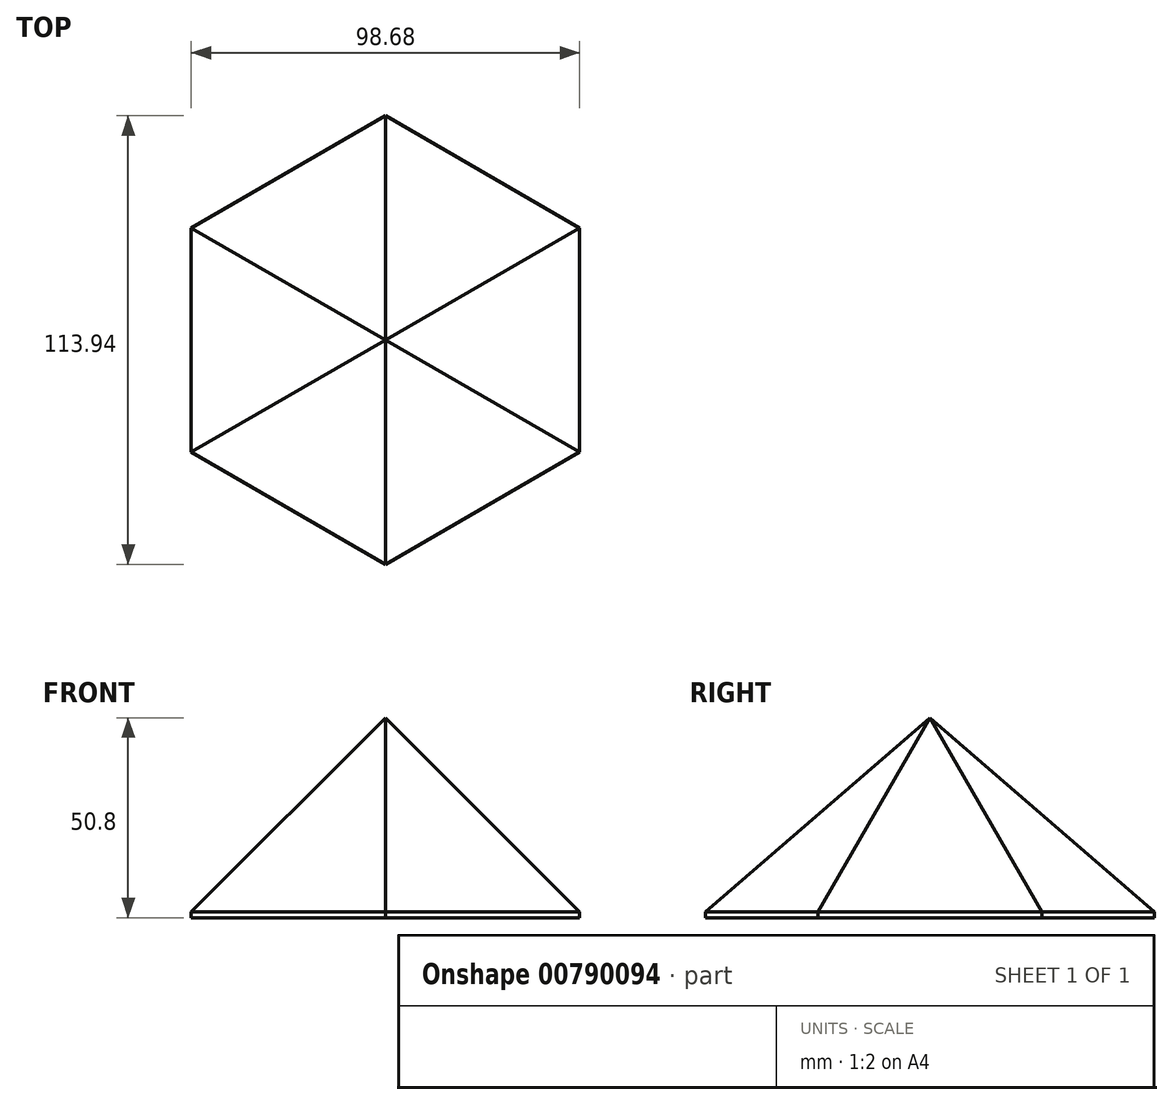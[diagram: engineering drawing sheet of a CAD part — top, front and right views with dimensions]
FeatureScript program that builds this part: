
annotation { "Feature Type Name" : "Feature", "Feature Type Description" : "" }
export const myFeature = defineFeature(function(context is Context, id is Id, definition is map)
    precondition{}
    {
        {
            var Q0;
            Q0=qCreatedBy(makeId("Top.planeOp"),FACE);
            var sketch = newSketch(context, id + "F0", { "sketchPlane" : qUnion([Q0])});
            skCircle(sketch, "E0.cCircle", {"center": v(0, 0) * mm, "radius": 49.34 * mm, "construction": true});
            skLineSegment(sketch, "E0.0", {"start": v(49.34, 28.49) * mm, "end": v(49.34, -28.49) * mm});
            skLineSegment(sketch, "E0.1", {"start": v(49.34, -28.49) * mm, "end": v(0, -56.97) * mm});
            skLineSegment(sketch, "E0.2", {"start": v(0, -56.97) * mm, "end": v(-49.34, -28.49) * mm});
            skLineSegment(sketch, "E0.3", {"start": v(-49.34, -28.49) * mm, "end": v(-49.34, 28.49) * mm});
            skLineSegment(sketch, "E0.4", {"start": v(-49.34, 28.49) * mm, "end": v(0, 56.97) * mm});
            skLineSegment(sketch, "E0.5", {"start": v(0, 56.97) * mm, "end": v(49.34, 28.49) * mm});
            skPoint(sketch, "E0.0.midPoint", {"position": v(49.34, 0) * mm});
            skLineSegment(sketch, "E1", {"start": v(-75.74, 0) * mm, "end": v(75.74, 0) * mm});
            skLineSegment(sketch, "E2", {"start": v(-51.85, 0) * mm, "end": v(-12.8, 67.78) * mm, "construction": true});
            skLineSegment(sketch, "E3", {"start": v(-12.8, 67.78) * mm, "end": v(-4.08, 55.46) * mm, "construction": true});
            skLineSegment(sketch, "E4", {"start": v(-4.08, 55.46) * mm, "end": v(-12.99, 21.33) * mm, "construction": true});
            skLineSegment(sketch, "E5", {"start": v(-12.99, 21.33) * mm, "end": v(13.18, -4.27) * mm, "construction": true});
            skLineSegment(sketch, "E6", {"start": v(13.18, -4.27) * mm, "end": v(14.7, -39.91) * mm, "construction": true});
            skLineSegment(sketch, "E7", {"start": v(14.7, -39.91) * mm, "end": v(-39.9, -36.3) * mm, "construction": true});
            skSolve(sketch);
        }
        {
            var Q0;
            Q0=makeQuery(id+"F0.imprint","IMPRINT",FACE,{"disambiguationData":[TD([[makeQuery(id+"F0.imprint","IMPRINT",EDGE,{"derivedFrom":sQuery(id+"F0.wireOp",EDGE,"E0.0")}),-1.0]])]});
            extrude(context, id + "F1", {"entities" : qUnion([Q0]), "depth" : 50.8 * mm, "offsetDistance" : 25.4 * mm});
        }
        {
            var Q0;
            Q0=makeQuery(id+"F1.opExtrude","CAP_EDGE",EDGE,{"disambiguationData":[OSD([sQuery(id+"F0.wireOp",EDGE,"E0.1")])],"isStart":false});
            var Q1;
            Q1=makeQuery(id+"F1.opExtrude","CAP_EDGE",EDGE,{"disambiguationData":[OSD([sQuery(id+"F0.wireOp",EDGE,"E0.0")])],"isStart":false});
            var Q2;
            Q2=makeQuery(id+"F1.opExtrude","CAP_EDGE",EDGE,{"disambiguationData":[OSD([sQuery(id+"F0.wireOp",EDGE,"E0.5")])],"isStart":false});
            var Q3;
            Q3=makeQuery(id+"F1.opExtrude","CAP_EDGE",EDGE,{"disambiguationData":[OSD([sQuery(id+"F0.wireOp",EDGE,"E0.4")])],"isStart":false});
            var Q4;
            Q4=makeQuery(id+"F1.opExtrude","CAP_EDGE",EDGE,{"disambiguationData":[OSD([sQuery(id+"F0.wireOp",EDGE,"E0.3")])],"isStart":false});
            var Q5;
            Q5=makeQuery(id+"F1.opExtrude","CAP_EDGE",EDGE,{"disambiguationData":[OSD([sQuery(id+"F0.wireOp",EDGE,"E0.2")])],"isStart":false});
            chamfer(context, id + "F2", {"entities" : qUnion([Q0, Q1, Q2, Q3, Q4, Q5]), "width" : 49.34 * mm, "tangentPropagation" : true});
        }
    });
